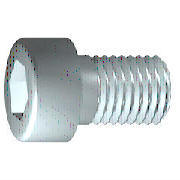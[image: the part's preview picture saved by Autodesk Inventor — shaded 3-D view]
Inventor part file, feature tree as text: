
AUTODESK INVENTOR PART (.ipt)
format: ipt  version: 2024.2 (Build 282272000, 272)  size: 201,216 bytes
history: native  units: mm (DEFAULTED — no unit token found)
features: extrude x1, plane x1, fillet x1
ambient origin geometry x7: Origin, YZ Plane, XY Plane, X Axis, Y Axis, Z Axis, Center Point
bodies: Solid1 (feature_tree), Body (feature_tree)
feature tree (3):
  extrude  "Slot"  Depth=6.75mm
  plane  "Work Plane1"
  fillet  "Fillet2"  Radius=0.306825mm
